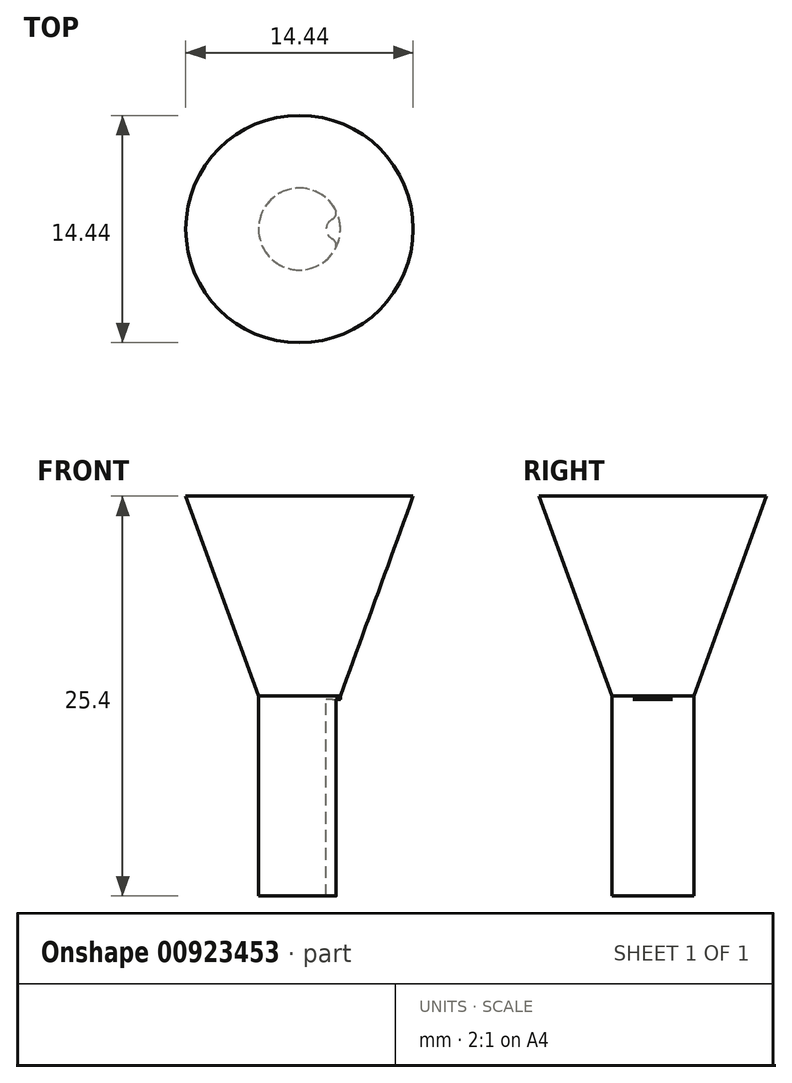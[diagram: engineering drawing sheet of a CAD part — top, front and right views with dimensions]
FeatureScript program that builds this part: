
annotation { "Feature Type Name" : "Feature", "Feature Type Description" : "" }
export const myFeature = defineFeature(function(context is Context, id is Id, definition is map)
    precondition{}
    {
        {
            var Q0;
            Q0=qCreatedBy(makeId("Top.planeOp"),FACE);
            var sketch = newSketch(context, id + "F0", { "sketchPlane" : qUnion([Q0])});
            skLineSegment(sketch, "E0", {"start": v(0, 0) * mm, "end": v(2.4, 0) * mm, "construction": true});
            skPoint(sketch, "E1.visualSharp", {"position": v(2.23, 0.88) * mm});
            skPoint(sketch, "E2.visualSharp", {"position": v(2.23, -0.88) * mm});
            skArc(sketch, "E3.0", {"start": v(2.28, 1.25) * mm, "mid": v(-2.6, 0) * mm, "end": v(2.28, -1.25) * mm});
            skArc(sketch, "E4", {"start": v(2.09, 0.63) * mm, "mid": v(1.7, 0) * mm, "end": v(2.09, -0.63) * mm});
            skArc(sketch, "E5", {"start": v(2.09, 0.63) * mm, "mid": v(2.32, 0.9) * mm, "end": v(2.28, 1.25) * mm});
            skArc(sketch, "E6", {"start": v(2.28, -1.25) * mm, "mid": v(2.32, -0.9) * mm, "end": v(2.09, -0.63) * mm});
            skSolve(sketch);
        }
        {
            var Q0;
            Q0 = qSketchRegion(id + "F0", true);
            extrude(context, id + "F1", {"entities" : qUnion([Q0]), "oppositeDirection" : true, "depth" : 12.7 * mm, "offsetDistance" : 25.4 * mm});
        }
        {
            var Q0;
            Q0=qCreatedBy(makeId("Top.planeOp"),FACE);
            var sketch = newSketch(context, id + "F2", { "sketchPlane" : qUnion([Q0])});
            skCircle(sketch, "E7", {"center": v(0, 0) * mm, "radius": 2.6 * mm});
            skSolve(sketch);
        }
        {
            var Q0;
            Q0=makeQuery(id+"F2.imprint","IMPRINT",FACE,{"disambiguationData":[TD([[makeQuery(id+"F2.imprint","IMPRINT",EDGE,{"derivedFrom":sQuery(id+"F2.wireOp",EDGE,"E7")}),1.0]])]});
            extrude(context, id + "F3", {"entities" : qUnion([Q0]), "operationType" : NewBodyOperationType.ADD, "depth" : 12.7 * mm, "offsetDistance" : 25.4 * mm, "hasDraft" : true, "draftAngle" : 20 * degree});
        }
        {
            var Q0;
            Q0=qCreatedBy(makeId("Top.planeOp"),FACE);
            var sketch = newSketch(context, id + "F4", { "sketchPlane" : qUnion([Q0])});
            skCircle(sketch, "E8", {"center": v(0, 0) * mm, "radius": 2.4 * mm});
            skSolve(sketch);
        }
        {
            var Q0;
            {var subQ0=sQuery(id+"F2.wireOp",EDGE,"E7");Q0=makeQuery(id+"F3.boolean.opBoolean","SPLIT",FACE,{"disambiguationData":[TD([makeQuery(id+"F1.opExtrude","SWEPT_FACE",FACE,{"disambiguationData":[OSD([sQuery(id+"F0.wireOp",EDGE,"E3.0")])]})])],"derivedFrom":makeQuery(id+"F3.opExtrude","CAP_FACE",FACE,{"disambiguationData":[OSD([subQ0])],"isStart":true})});}
            var sketch = newSketch(context, id + "F5", { "sketchPlane" : qUnion([Q0])});
            skArc(sketch, "E9", {"start": v(2.09, 0.63) * mm, "mid": v(1.7, 0) * mm, "end": v(2.09, -0.63) * mm});
            skArc(sketch, "E10", {"start": v(2.09, 0.63) * mm, "mid": v(2.32, 0.9) * mm, "end": v(2.28, 1.25) * mm});
            skArc(sketch, "E11", {"start": v(2.28, -1.25) * mm, "mid": v(2.32, -0.9) * mm, "end": v(2.09, -0.63) * mm});
            skArc(sketch, "E12", {"start": v(2.28, -1.25) * mm, "mid": v(2.6, 0) * mm, "end": v(2.28, 1.25) * mm});
            skSolve(sketch);
        }
        {
            var Q0;
            Q0 = qSketchRegion(id + "F5", true);
            extrude(context, id + "F6", {"entities" : qUnion([Q0]), "operationType" : NewBodyOperationType.ADD, "depth" : .2 * mm, "offsetDistance" : 25.4 * mm});
        }
    });
